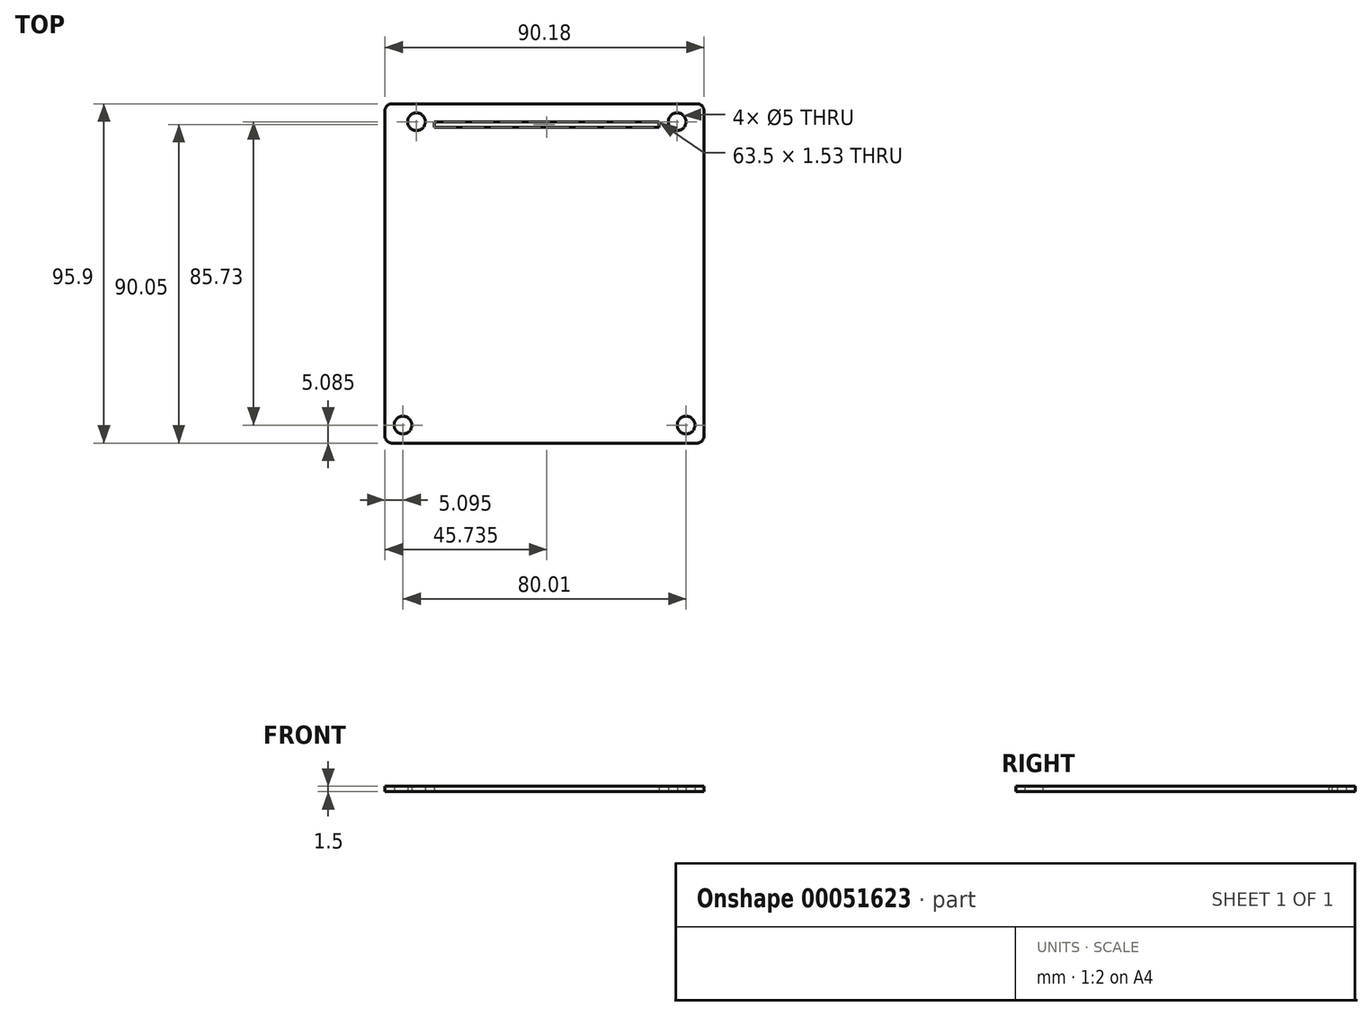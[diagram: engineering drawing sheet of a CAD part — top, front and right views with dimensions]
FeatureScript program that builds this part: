
annotation { "Feature Type Name" : "Feature", "Feature Type Description" : "" }
export const myFeature = defineFeature(function(context is Context, id is Id, definition is map)
    precondition{}
    {
        {
            var Q0;
            Q0=qCreatedBy(makeId("Top.planeOp"),FACE);
            var sketch = newSketch(context, id + "F0", { "sketchPlane" : qUnion([Q0])});
            skLineSegment(sketch, "E0.rect.bottom", {"start": v(43.09, 47.94) * mm, "end": v(-43.09, 47.94) * mm});
            skLineSegment(sketch, "E0.rect.top", {"start": v(43.09, -47.95) * mm, "end": v(-43.08, -47.95) * mm});
            skLineSegment(sketch, "E0.rect.left", {"start": v(45.09, 45.94) * mm, "end": v(45.09, -45.95) * mm});
            skLineSegment(sketch, "E0.rect.right", {"start": v(-45.09, 45.94) * mm, "end": v(-45.09, -45.95) * mm});
            skPoint(sketch, "E0.rect.middle", {"position": v(0, 0) * mm});
            skPoint(sketch, "E1.visualSharp", {"position": v(-45.09, 47.94) * mm});
            skArc(sketch, "E1.filletArc", {"start": v(-43.09, 47.94) * mm, "mid": v(-44.5, 47.36) * mm, "end": v(-45.09, 45.94) * mm});
            skPoint(sketch, "E2.visualSharp", {"position": v(45.09, 47.94) * mm});
            skArc(sketch, "E2.filletArc", {"start": v(45.09, 45.94) * mm, "mid": v(44.5, 47.36) * mm, "end": v(43.09, 47.94) * mm});
            skPoint(sketch, "E3.visualSharp", {"position": v(45.09, -47.95) * mm});
            skArc(sketch, "E3.filletArc", {"start": v(43.09, -47.95) * mm, "mid": v(44.5, -47.36) * mm, "end": v(45.09, -45.95) * mm});
            skPoint(sketch, "E4.visualSharp", {"position": v(-45.09, -47.95) * mm});
            skArc(sketch, "E4.filletArc", {"start": v(-45.08, -45.95) * mm, "mid": v(-44.5, -47.36) * mm, "end": v(-43.08, -47.95) * mm});
            skPoint(sketch, "E5", {"position": v(-40, -42.87) * mm});
            skPoint(sketch, "E6", {"position": v(-36.18, 42.86) * mm});
            skPoint(sketch, "E7", {"position": v(37.48, 42.86) * mm});
            skPoint(sketch, "E8", {"position": v(40.02, -42.87) * mm});
            skLineSegment(sketch, "E9.bottom", {"start": v(-31.1, 42.86) * mm, "end": v(32.4, 42.86) * mm});
            skLineSegment(sketch, "E9.top", {"start": v(-31.1, 41.34) * mm, "end": v(32.4, 41.34) * mm});
            skLineSegment(sketch, "E9.left", {"start": v(-31.1, 42.86) * mm, "end": v(-31.1, 41.34) * mm});
            skLineSegment(sketch, "E9.right", {"start": v(32.4, 42.86) * mm, "end": v(32.4, 41.34) * mm});
            skSolve(sketch);
        }
        {
            var Q0;
            Q0=makeQuery(id+"F0.imprint","IMPRINT",FACE,{"disambiguationData":[TD([[makeQuery(id+"F0.imprint","IMPRINT",EDGE,{"derivedFrom":sQuery(id+"F0.wireOp",EDGE,"E0.rect.bottom")}),1.0]])]});
            extrude(context, id + "F1", {"entities" : qUnion([Q0]), "depth" : 1.5 * mm});
        }
        {
            var Q0;
            Q0=sQuery(id+"F0.wireOp",VERTEX,"E6");
            var Q1;
            Q1=sQuery(id+"F0.wireOp",VERTEX,"E7");
            var Q2;
            Q2=sQuery(id+"F0.wireOp",VERTEX,"E8");
            var Q3;
            Q3=sQuery(id+"F0.wireOp",VERTEX,"E5");
            var Q4;
            Q4=makeQuery(id+"F1.opExtrude","SWEPT_BODY",BODY,{"disambiguationData":[OSD([sQuery(id+"F0.wireOp",EDGE,"E0.rect.bottom"),sQuery(id+"F0.wireOp",EDGE,"E0.rect.top"),sQuery(id+"F0.wireOp",EDGE,"E0.rect.left"),sQuery(id+"F0.wireOp",EDGE,"E0.rect.right"),sQuery(id+"F0.wireOp",EDGE,"E1.filletArc"),sQuery(id+"F0.wireOp",EDGE,"E2.filletArc"),sQuery(id+"F0.wireOp",EDGE,"E3.filletArc"),sQuery(id+"F0.wireOp",EDGE,"E4.filletArc")])]});
            hole(context, id + "F2", {"style" : HoleStyle.SIMPLE, "holeDiameter" : 5 * mm, "endStyle" : HoleEndStyle.THROUGH, "oppositeDirection" : true, "locations" : qUnion([Q0, Q1, Q2, Q3]), "scope" : qUnion([Q4])});
        }
    });
